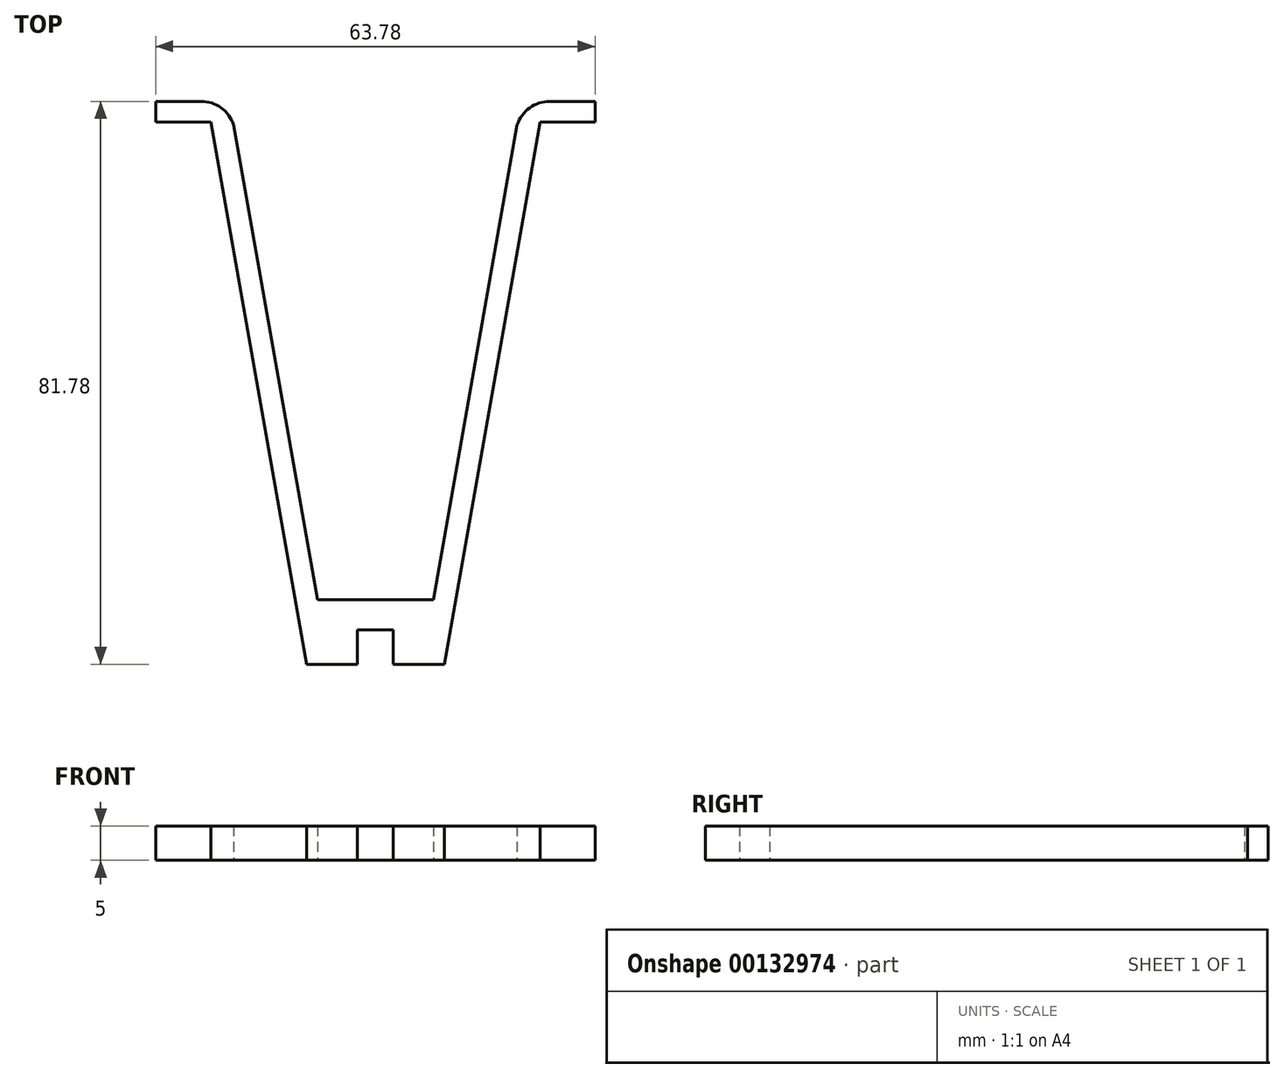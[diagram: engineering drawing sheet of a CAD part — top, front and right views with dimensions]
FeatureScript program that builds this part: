
annotation { "Feature Type Name" : "Feature", "Feature Type Description" : "" }
export const myFeature = defineFeature(function(context is Context, id is Id, definition is map)
    precondition{}
    {
        {
            var Q0;
            Q0=qCreatedBy(makeId("Top.planeOp"),FACE);
            var sketch = newSketch(context, id + "F0", { "sketchPlane" : qUnion([Q0])});
            skLineSegment(sketch, "E0", {"start": v(-2.6, 0) * mm, "end": v(-10, 0) * mm});
            skLineSegment(sketch, "E1", {"start": v(-10, 0) * mm, "end": v(-23.9, 78.78) * mm});
            skLineSegment(sketch, "E2", {"start": v(-20.58, 78.33) * mm, "end": v(-8.42, 9.4) * mm});
            skLineSegment(sketch, "E3.MirrorCS", {"start": v(20.58, 78.33) * mm, "end": v(8.42, 9.4) * mm});
            skLineSegment(sketch, "E4.MirrorCS", {"start": v(10, 0) * mm, "end": v(23.9, 78.78) * mm});
            skLineSegment(sketch, "E5.MirrorCS", {"start": v(8.42, 9.4) * mm, "end": v(3.42, 9.4) * mm});
            skLineSegment(sketch, "E6.MirrorCS", {"start": v(2.6, 0) * mm, "end": v(10, 0) * mm});
            skLineSegment(sketch, "E7", {"start": v(-2.6, 5) * mm, "end": v(-2.6, 0) * mm});
            skPoint(sketch, "E8.end.orphan", {"position": v(0, 5) * mm});
            skPoint(sketch, "E9.MirrorCS.end.orphan", {"position": v(2.6, 5) * mm});
            skPoint(sketch, "E9.MirrorCS.start.orphan", {"position": v(3.42, 9.4) * mm});
            skLineSegment(sketch, "E10", {"start": v(-2.6, 5) * mm, "end": v(0, 5) * mm});
            skPoint(sketch, "E11.end.orphan", {"position": v(-3.42, 9.4) * mm});
            skLineSegment(sketch, "E12", {"start": v(-8.42, 9.4) * mm, "end": v(0, 9.4) * mm});
            skLineSegment(sketch, "E13.MirrorCS", {"start": v(8.42, 9.4) * mm, "end": v(0, 9.4) * mm});
            skLineSegment(sketch, "E14.MirrorCS", {"start": v(2.6, 5) * mm, "end": v(2.6, 0) * mm});
            skLineSegment(sketch, "E15.MirrorCS", {"start": v(2.6, 5) * mm, "end": v(0, 5) * mm});
            skPoint(sketch, "E16.orphan", {"position": v(0, 0) * mm});
            skLineSegment(sketch, "E17", {"start": v(-23.9, 78.78) * mm, "end": v(-31.9, 78.78) * mm});
            skLineSegment(sketch, "E18", {"start": v(-31.9, 78.78) * mm, "end": v(-31.9, 81.78) * mm});
            skLineSegment(sketch, "E19", {"start": v(-31.9, 81.78) * mm, "end": v(-20.58, 81.78) * mm});
            skLineSegment(sketch, "E20", {"start": v(-20.58, 81.78) * mm, "end": v(-20.58, 78.33) * mm});
            skLineSegment(sketch, "E21.MirrorCS", {"start": v(23.9, 78.78) * mm, "end": v(31.9, 78.78) * mm});
            skLineSegment(sketch, "E22.MirrorCS", {"start": v(31.9, 81.78) * mm, "end": v(20.58, 81.78) * mm});
            skLineSegment(sketch, "E23.MirrorCS", {"start": v(20.58, 81.78) * mm, "end": v(20.58, 78.33) * mm});
            skLineSegment(sketch, "E24.MirrorCS", {"start": v(31.9, 78.78) * mm, "end": v(31.9, 81.78) * mm});
            skPoint(sketch, "E25.MirrorCS.end.orphan", {"position": v(20.58, 78.33) * mm});
            skPoint(sketch, "E25.MirrorCS.start.orphan", {"position": v(23.9, 78.78) * mm});
            skSolve(sketch);
        }
        {
            var Q0;
            Q0=makeQuery(id+"F0.imprint","IMPRINT",FACE,{"disambiguationData":[TD([[makeQuery(id+"F0.imprint","IMPRINT",EDGE,{"derivedFrom":sQuery(id+"F0.wireOp",EDGE,"E0")}),-1.0]])]});
            extrude(context, id + "F1", {"entities" : qUnion([Q0]), "depth" : 5 * mm});
        }
        {
            var Q0;
            Q0=makeQuery(id+"F1.opExtrude","SWEPT_EDGE",EDGE,{"disambiguationData":[OSD([sQuery(id+"F0.wireOp",EDGE,"E19"),sQuery(id+"F0.wireOp",EDGE,"E20")])]});
            var Q1;
            Q1=makeQuery(id+"F1.opExtrude","SWEPT_EDGE",EDGE,{"disambiguationData":[OSD([sQuery(id+"F0.wireOp",EDGE,"E22.MirrorCS"),sQuery(id+"F0.wireOp",EDGE,"E23.MirrorCS")])]});
            fillet(context, id + "F2", {"entities" : qUnion([Q0, Q1]), "radius" : 5 * mm, "tangentPropagation" : true, "allowEdgeOverflow" : false});
        }
    });
